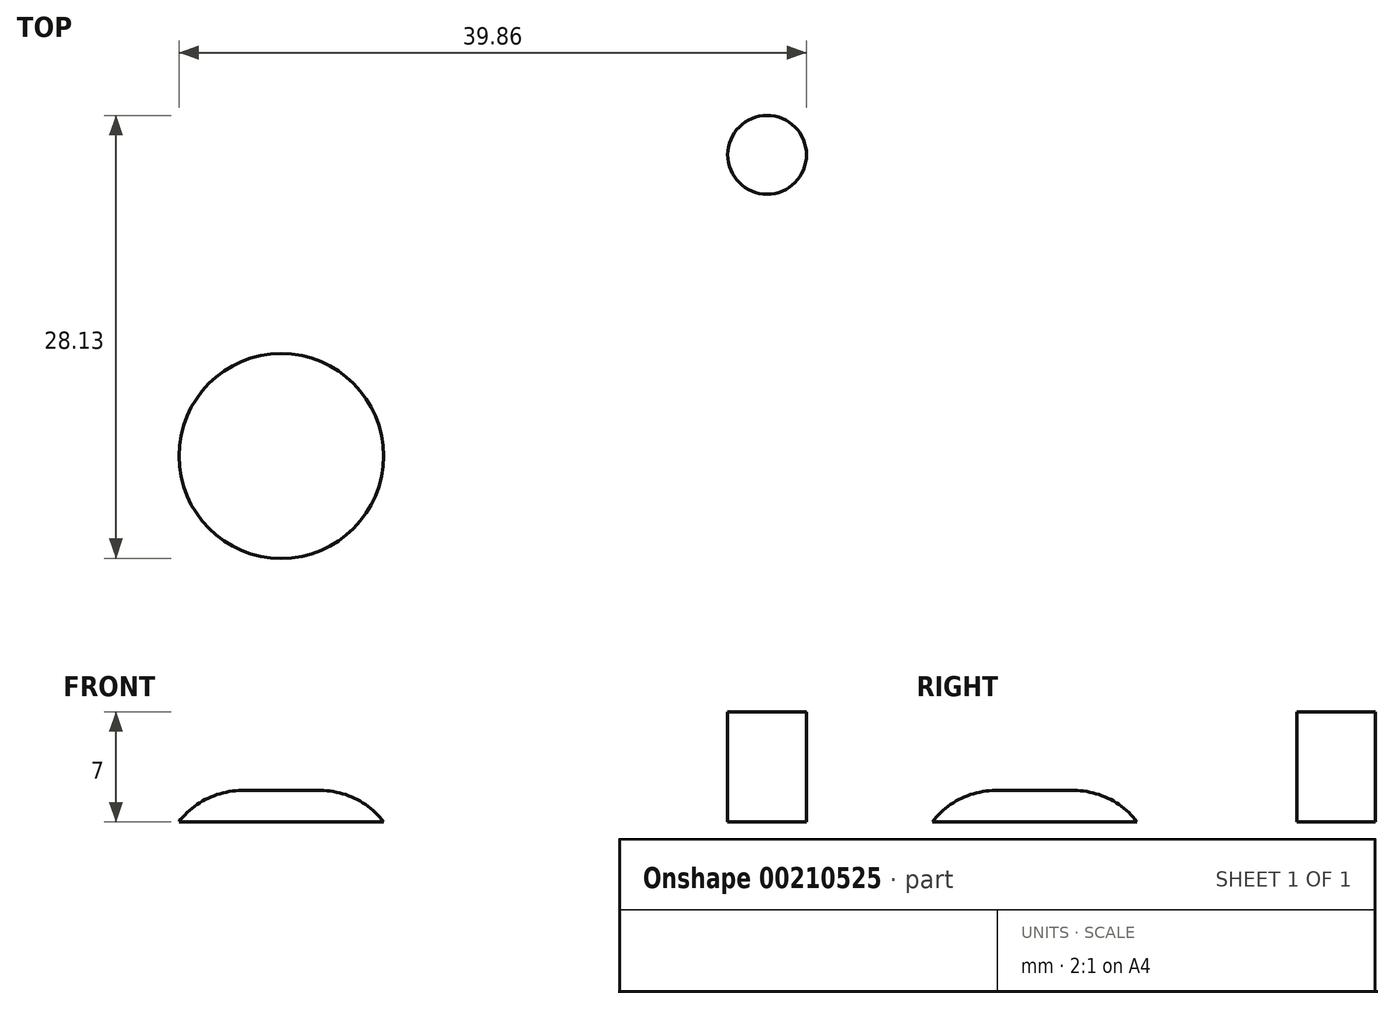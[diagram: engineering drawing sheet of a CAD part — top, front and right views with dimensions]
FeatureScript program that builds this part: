
annotation { "Feature Type Name" : "Feature", "Feature Type Description" : "" }
export const myFeature = defineFeature(function(context is Context, id is Id, definition is map)
    precondition{}
    {
        {
            var Q0;
            Q0=qCreatedBy(makeId("Top.planeOp"),FACE);
            var sketch = newSketch(context, id + "F0", { "sketchPlane" : qUnion([Q0])});
            skCircle(sketch, "E0", {"center": v(0, 0) * mm, "radius": 6.5 * mm});
            skSolve(sketch);
        }
        {
            var Q0;
            Q0=makeQuery(id+"F0.imprint","IMPRINT",FACE,{"disambiguationData":[TD([[makeQuery(id+"F0.imprint","IMPRINT",EDGE,{"derivedFrom":sQuery(id+"F0.wireOp",EDGE,"E0")}),1.0]])]});
            extrude(context, id + "F1", {"entities" : qUnion([Q0]), "depth" : 2 * mm});
        }
        {
            var Q0;
            Q0=makeQuery(id+"F1.opExtrude","CAP_EDGE",EDGE,{"disambiguationData":[OSD([sQuery(id+"F0.wireOp",EDGE,"E0")])],"isStart":false});
            fillet(context, id + "F2", {"entities" : qUnion([Q0]), "radius" : 5 * mm, "tangentPropagation" : true, "allowEdgeOverflow" : false});
        }
        {
            var Q0;
            Q0=qCreatedBy(makeId("Top.planeOp"),FACE);
            var sketch = newSketch(context, id + "F3", { "sketchPlane" : qUnion([Q0])});
            skCircle(sketch, "E1", {"center": v(30.86, 19.13) * mm, "radius": 2.5 * mm});
            skSolve(sketch);
        }
        {
            var Q0;
            Q0=makeQuery(id+"F3.imprint","IMPRINT",FACE,{"disambiguationData":[TD([[makeQuery(id+"F3.imprint","IMPRINT",EDGE,{"derivedFrom":sQuery(id+"F3.wireOp",EDGE,"E1")}),1.0]])]});
            extrude(context, id + "F4", {"entities" : qUnion([Q0]), "depth" : 7 * mm});
        }
    });
